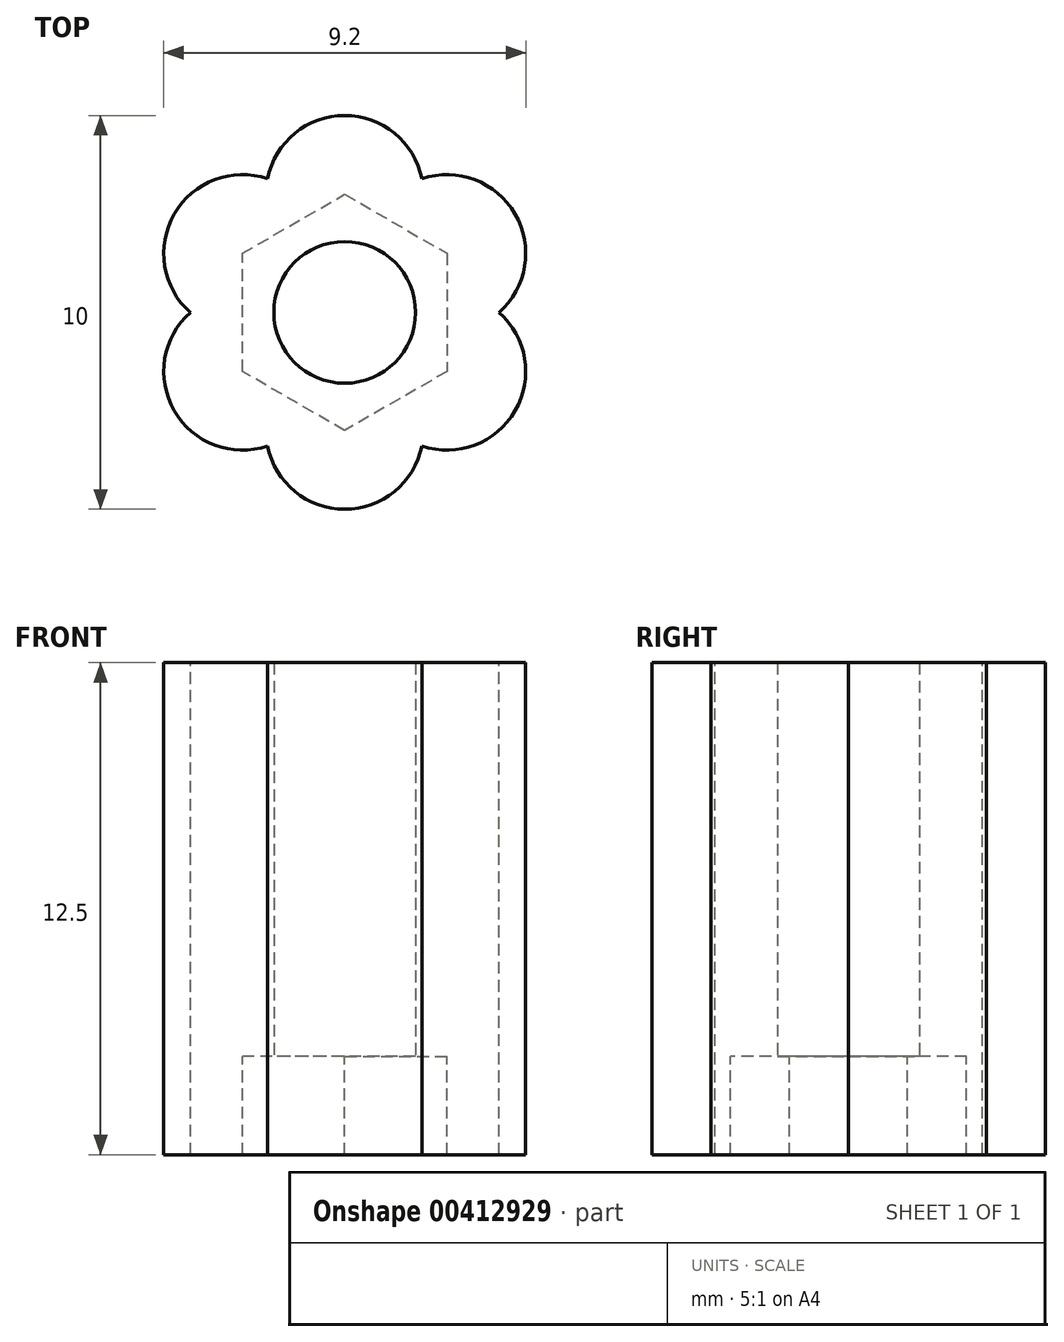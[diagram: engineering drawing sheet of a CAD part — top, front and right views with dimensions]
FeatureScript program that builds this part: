
annotation { "Feature Type Name" : "Feature", "Feature Type Description" : "" }
export const myFeature = defineFeature(function(context is Context, id is Id, definition is map)
    precondition{}
    {
        {
            var Q0;
            Q0=qCreatedBy(makeId("Top.planeOp"),FACE);
            var sketch = newSketch(context, id + "F0", { "sketchPlane" : qUnion([Q0])});
            skCircle(sketch, "E0.cCircle", {"center": v(0, 0) * mm, "radius": 3 * mm, "construction": true});
            skLineSegment(sketch, "E0.0", {"start": v(0, 3) * mm, "end": v(2.6, 1.5) * mm});
            skLineSegment(sketch, "E0.1", {"start": v(2.6, 1.5) * mm, "end": v(2.6, -1.5) * mm});
            skLineSegment(sketch, "E0.2", {"start": v(2.6, -1.5) * mm, "end": v(0, -3) * mm});
            skLineSegment(sketch, "E0.3", {"start": v(0, -3) * mm, "end": v(-2.6, -1.5) * mm});
            skLineSegment(sketch, "E0.4", {"start": v(-2.6, -1.5) * mm, "end": v(-2.6, 1.5) * mm});
            skLineSegment(sketch, "E0.5", {"start": v(-2.6, 1.5) * mm, "end": v(0, 3) * mm});
            skCircle(sketch, "E1", {"center": v(0, 0) * mm, "radius": 1.8 * mm});
            skCircle(sketch, "E2", {"center": v(0, 3) * mm, "radius": 2 * mm});
            skCircle(sketch, "E3", {"center": v(2.6, 1.5) * mm, "radius": 2 * mm});
            skCircle(sketch, "E4", {"center": v(2.6, -1.5) * mm, "radius": 2 * mm});
            skCircle(sketch, "E5", {"center": v(0, -3) * mm, "radius": 2 * mm});
            skCircle(sketch, "E6", {"center": v(-2.6, -1.5) * mm, "radius": 2 * mm});
            skCircle(sketch, "E7", {"center": v(-2.6, 1.5) * mm, "radius": 2 * mm});
            skSolve(sketch);
        }
        {
            var Q0;
            {var subQ3=sQuery(id+"F0.wireOp",EDGE,"E0.0");var subQ7=sQuery(id+"F0.wireOp",EDGE,"E0.5");var subQ9=makeQuery(id+"F0.imprint","INTERSECT",VERTEX,{"derivedFrom":[subQ3,subQ7]});Q0=makeQuery(id+"F0.imprint","IMPRINT",FACE,{"disambiguationData":[TD([[makeQuery(id+"F0.imprint","IMPRINT",EDGE,{"disambiguationData":[TD([[subQ9,-1.0]])],"derivedFrom":subQ3}),1.0]])]});}
            var Q1;
            {var subQ0=sQuery(id+"F0.wireOp",EDGE,"E3");var subQ1=sQuery(id+"F0.wireOp",EDGE,"E0.0");var subQ2=makeQuery(id+"F0.imprint","INTERSECT",VERTEX,{"derivedFrom":[subQ1,subQ0]});Q1=makeQuery(id+"F0.imprint","IMPRINT",FACE,{"disambiguationData":[TD([[makeQuery(id+"F0.imprint","IMPRINT",EDGE,{"disambiguationData":[TD([[subQ2,-1.0]])],"derivedFrom":subQ1}),1.0]])]});}
            var Q2;
            {var subQ0=sQuery(id+"F0.wireOp",EDGE,"E2");var subQ1=sQuery(id+"F0.wireOp",EDGE,"E0.5");var subQ2=makeQuery(id+"F0.imprint","INTERSECT",VERTEX,{"derivedFrom":[subQ1,subQ0]});Q2=makeQuery(id+"F0.imprint","IMPRINT",FACE,{"disambiguationData":[TD([[makeQuery(id+"F0.imprint","IMPRINT",EDGE,{"disambiguationData":[TD([[subQ2,-1.0]])],"derivedFrom":subQ1}),1.0]])]});}
            var Q3;
            {var subQ3=sQuery(id+"F0.wireOp",EDGE,"E0.5");var subQ7=sQuery(id+"F0.wireOp",EDGE,"E0.4");var subQ9=makeQuery(id+"F0.imprint","INTERSECT",VERTEX,{"derivedFrom":[subQ7,subQ3]});Q3=makeQuery(id+"F0.imprint","IMPRINT",FACE,{"disambiguationData":[TD([[makeQuery(id+"F0.imprint","IMPRINT",EDGE,{"disambiguationData":[TD([[subQ9,1.0]])],"derivedFrom":subQ7}),1.0]])]});}
            var Q4;
            {var subQ0=sQuery(id+"F0.wireOp",EDGE,"E7");var subQ1=sQuery(id+"F0.wireOp",EDGE,"E0.4");var subQ2=makeQuery(id+"F0.imprint","INTERSECT",VERTEX,{"derivedFrom":[subQ1,subQ0]});Q4=makeQuery(id+"F0.imprint","IMPRINT",FACE,{"disambiguationData":[TD([[makeQuery(id+"F0.imprint","IMPRINT",EDGE,{"disambiguationData":[TD([[subQ2,-1.0]])],"derivedFrom":subQ1}),1.0]])]});}
            var Q5;
            {var subQ3=sQuery(id+"F0.wireOp",EDGE,"E0.3");var subQ5=sQuery(id+"F0.wireOp",EDGE,"E0.4");var subQ6=makeQuery(id+"F0.imprint","INTERSECT",VERTEX,{"derivedFrom":[subQ3,subQ5]});Q5=makeQuery(id+"F0.imprint","IMPRINT",FACE,{"disambiguationData":[TD([[makeQuery(id+"F0.imprint","IMPRINT",EDGE,{"disambiguationData":[TD([[subQ6,1.0]])],"derivedFrom":subQ3}),1.0]])]});}
            var Q6;
            {var subQ0=sQuery(id+"F0.wireOp",EDGE,"E6");var subQ1=sQuery(id+"F0.wireOp",EDGE,"E0.3");var subQ2=makeQuery(id+"F0.imprint","INTERSECT",VERTEX,{"derivedFrom":[subQ1,subQ0]});Q6=makeQuery(id+"F0.imprint","IMPRINT",FACE,{"disambiguationData":[TD([[makeQuery(id+"F0.imprint","IMPRINT",EDGE,{"disambiguationData":[TD([[subQ2,-1.0]])],"derivedFrom":subQ1}),1.0]])]});}
            var Q7;
            {var subQ5=sQuery(id+"F0.wireOp",EDGE,"E0.2");var subQ7=sQuery(id+"F0.wireOp",EDGE,"E0.3");var subQ8=makeQuery(id+"F0.imprint","INTERSECT",VERTEX,{"derivedFrom":[subQ5,subQ7]});Q7=makeQuery(id+"F0.imprint","IMPRINT",FACE,{"disambiguationData":[TD([[makeQuery(id+"F0.imprint","IMPRINT",EDGE,{"disambiguationData":[TD([[subQ8,1.0]])],"derivedFrom":subQ5}),1.0]])]});}
            var Q8;
            {var subQ0=sQuery(id+"F0.wireOp",EDGE,"E5");var subQ1=sQuery(id+"F0.wireOp",EDGE,"E0.2");var subQ2=makeQuery(id+"F0.imprint","INTERSECT",VERTEX,{"derivedFrom":[subQ1,subQ0]});Q8=makeQuery(id+"F0.imprint","IMPRINT",FACE,{"disambiguationData":[TD([[makeQuery(id+"F0.imprint","IMPRINT",EDGE,{"disambiguationData":[TD([[subQ2,-1.0]])],"derivedFrom":subQ1}),1.0]])]});}
            var Q9;
            {var subQ5=sQuery(id+"F0.wireOp",EDGE,"E0.1");var subQ7=sQuery(id+"F0.wireOp",EDGE,"E0.2");var subQ8=makeQuery(id+"F0.imprint","INTERSECT",VERTEX,{"derivedFrom":[subQ5,subQ7]});Q9=makeQuery(id+"F0.imprint","IMPRINT",FACE,{"disambiguationData":[TD([[makeQuery(id+"F0.imprint","IMPRINT",EDGE,{"disambiguationData":[TD([[subQ8,1.0]])],"derivedFrom":subQ5}),1.0]])]});}
            var Q10;
            {var subQ0=sQuery(id+"F0.wireOp",EDGE,"E4");var subQ1=sQuery(id+"F0.wireOp",EDGE,"E0.1");var subQ2=makeQuery(id+"F0.imprint","INTERSECT",VERTEX,{"derivedFrom":[subQ1,subQ0]});Q10=makeQuery(id+"F0.imprint","IMPRINT",FACE,{"disambiguationData":[TD([[makeQuery(id+"F0.imprint","IMPRINT",EDGE,{"disambiguationData":[TD([[subQ2,-1.0]])],"derivedFrom":subQ1}),1.0]])]});}
            var Q11;
            {var subQ5=sQuery(id+"F0.wireOp",EDGE,"E0.1");var subQ6=sQuery(id+"F0.wireOp",EDGE,"E0.0");var subQ7=makeQuery(id+"F0.imprint","INTERSECT",VERTEX,{"derivedFrom":[subQ6,subQ5]});Q11=makeQuery(id+"F0.imprint","IMPRINT",FACE,{"disambiguationData":[TD([[makeQuery(id+"F0.imprint","IMPRINT",EDGE,{"disambiguationData":[TD([[subQ7,1.0]])],"derivedFrom":subQ6}),1.0]])]});}
            extrude(context, id + "F1", {"entities" : qUnion([Q0, Q1, Q2, Q3, Q4, Q5, Q6, Q7, Q8, Q9, Q10, Q11]), "oppositeDirection" : true, "depth" : 2.5 * mm, "offsetDistance" : 25 * mm});
        }
        {
            var Q0;
            {var subQ5=sQuery(id+"F0.wireOp",EDGE,"E0.2");var subQ7=sQuery(id+"F0.wireOp",EDGE,"E0.3");var subQ8=makeQuery(id+"F0.imprint","INTERSECT",VERTEX,{"derivedFrom":[subQ5,subQ7]});Q0=makeQuery(id+"F0.imprint","IMPRINT",FACE,{"disambiguationData":[TD([[makeQuery(id+"F0.imprint","IMPRINT",EDGE,{"disambiguationData":[TD([[subQ8,1.0]])],"derivedFrom":subQ5}),1.0]])]});}
            var Q1;
            {var subQ0=sQuery(id+"F0.wireOp",EDGE,"E6");var subQ1=sQuery(id+"F0.wireOp",EDGE,"E0.3");var subQ2=makeQuery(id+"F0.imprint","INTERSECT",VERTEX,{"derivedFrom":[subQ1,subQ0]});Q1=makeQuery(id+"F0.imprint","IMPRINT",FACE,{"disambiguationData":[TD([[makeQuery(id+"F0.imprint","IMPRINT",EDGE,{"disambiguationData":[TD([[subQ2,-1.0]])],"derivedFrom":subQ1}),1.0]])]});}
            var Q2;
            {var subQ0=sQuery(id+"F0.wireOp",EDGE,"E5");var subQ1=sQuery(id+"F0.wireOp",EDGE,"E0.2");var subQ2=makeQuery(id+"F0.imprint","INTERSECT",VERTEX,{"derivedFrom":[subQ1,subQ0]});Q2=makeQuery(id+"F0.imprint","IMPRINT",FACE,{"disambiguationData":[TD([[makeQuery(id+"F0.imprint","IMPRINT",EDGE,{"disambiguationData":[TD([[subQ2,-1.0]])],"derivedFrom":subQ1}),1.0]])]});}
            var Q3;
            {var subQ5=sQuery(id+"F0.wireOp",EDGE,"E0.1");var subQ7=sQuery(id+"F0.wireOp",EDGE,"E0.2");var subQ8=makeQuery(id+"F0.imprint","INTERSECT",VERTEX,{"derivedFrom":[subQ5,subQ7]});Q3=makeQuery(id+"F0.imprint","IMPRINT",FACE,{"disambiguationData":[TD([[makeQuery(id+"F0.imprint","IMPRINT",EDGE,{"disambiguationData":[TD([[subQ8,1.0]])],"derivedFrom":subQ5}),1.0]])]});}
            var Q4;
            {var subQ0=sQuery(id+"F0.wireOp",EDGE,"E5");var subQ1=sQuery(id+"F0.wireOp",EDGE,"E0.2");var subQ2=makeQuery(id+"F0.imprint","INTERSECT",VERTEX,{"derivedFrom":[subQ1,subQ0]});Q4=makeQuery(id+"F0.imprint","IMPRINT",FACE,{"disambiguationData":[TD([[makeQuery(id+"F0.imprint","IMPRINT",EDGE,{"disambiguationData":[TD([[subQ2,-1.0]])],"derivedFrom":subQ1}),-1.0]])]});}
            var Q5;
            {var subQ1=sQuery(id+"F0.wireOp",EDGE,"E0.2");var subQ7=sQuery(id+"F0.wireOp",EDGE,"E0.3");var subQ8=makeQuery(id+"F0.imprint","INTERSECT",VERTEX,{"derivedFrom":[subQ1,subQ7]});Q5=makeQuery(id+"F0.imprint","IMPRINT",FACE,{"disambiguationData":[TD([[makeQuery(id+"F0.imprint","IMPRINT",EDGE,{"disambiguationData":[TD([[subQ8,1.0]])],"derivedFrom":subQ1}),-1.0]])]});}
            var Q6;
            {var subQ1=sQuery(id+"F0.wireOp",EDGE,"E0.1");var subQ6=sQuery(id+"F0.wireOp",EDGE,"E0.2");var subQ9=makeQuery(id+"F0.imprint","INTERSECT",VERTEX,{"derivedFrom":[subQ1,subQ6]});Q6=makeQuery(id+"F0.imprint","IMPRINT",FACE,{"disambiguationData":[TD([[makeQuery(id+"F0.imprint","IMPRINT",EDGE,{"disambiguationData":[TD([[subQ9,1.0]])],"derivedFrom":subQ1}),-1.0]])]});}
            var Q7;
            {var subQ0=sQuery(id+"F0.wireOp",EDGE,"E6");var subQ1=sQuery(id+"F0.wireOp",EDGE,"E0.3");var subQ2=makeQuery(id+"F0.imprint","INTERSECT",VERTEX,{"derivedFrom":[subQ1,subQ0]});Q7=makeQuery(id+"F0.imprint","IMPRINT",FACE,{"disambiguationData":[TD([[makeQuery(id+"F0.imprint","IMPRINT",EDGE,{"disambiguationData":[TD([[subQ2,-1.0]])],"derivedFrom":subQ1}),-1.0]])]});}
            var Q8;
            {var subQ3=sQuery(id+"F0.wireOp",EDGE,"E0.3");var subQ5=sQuery(id+"F0.wireOp",EDGE,"E0.4");var subQ6=makeQuery(id+"F0.imprint","INTERSECT",VERTEX,{"derivedFrom":[subQ3,subQ5]});Q8=makeQuery(id+"F0.imprint","IMPRINT",FACE,{"disambiguationData":[TD([[makeQuery(id+"F0.imprint","IMPRINT",EDGE,{"disambiguationData":[TD([[subQ6,1.0]])],"derivedFrom":subQ3}),1.0]])]});}
            var Q9;
            {var subQ1=sQuery(id+"F0.wireOp",EDGE,"E0.3");var subQ7=sQuery(id+"F0.wireOp",EDGE,"E0.4");var subQ8=makeQuery(id+"F0.imprint","INTERSECT",VERTEX,{"derivedFrom":[subQ1,subQ7]});Q9=makeQuery(id+"F0.imprint","IMPRINT",FACE,{"disambiguationData":[TD([[makeQuery(id+"F0.imprint","IMPRINT",EDGE,{"disambiguationData":[TD([[subQ8,1.0]])],"derivedFrom":subQ1}),-1.0]])]});}
            var Q10;
            {var subQ0=sQuery(id+"F0.wireOp",EDGE,"E4");var subQ1=sQuery(id+"F0.wireOp",EDGE,"E0.1");var subQ2=makeQuery(id+"F0.imprint","INTERSECT",VERTEX,{"derivedFrom":[subQ1,subQ0]});Q10=makeQuery(id+"F0.imprint","IMPRINT",FACE,{"disambiguationData":[TD([[makeQuery(id+"F0.imprint","IMPRINT",EDGE,{"disambiguationData":[TD([[subQ2,-1.0]])],"derivedFrom":subQ1}),1.0]])]});}
            var Q11;
            {var subQ5=sQuery(id+"F0.wireOp",EDGE,"E0.1");var subQ6=sQuery(id+"F0.wireOp",EDGE,"E0.0");var subQ7=makeQuery(id+"F0.imprint","INTERSECT",VERTEX,{"derivedFrom":[subQ6,subQ5]});Q11=makeQuery(id+"F0.imprint","IMPRINT",FACE,{"disambiguationData":[TD([[makeQuery(id+"F0.imprint","IMPRINT",EDGE,{"disambiguationData":[TD([[subQ7,1.0]])],"derivedFrom":subQ6}),1.0]])]});}
            var Q12;
            {var subQ0=sQuery(id+"F0.wireOp",EDGE,"E3");var subQ1=sQuery(id+"F0.wireOp",EDGE,"E0.0");var subQ2=makeQuery(id+"F0.imprint","INTERSECT",VERTEX,{"derivedFrom":[subQ1,subQ0]});Q12=makeQuery(id+"F0.imprint","IMPRINT",FACE,{"disambiguationData":[TD([[makeQuery(id+"F0.imprint","IMPRINT",EDGE,{"disambiguationData":[TD([[subQ2,-1.0]])],"derivedFrom":subQ1}),1.0]])]});}
            var Q13;
            {var subQ0=sQuery(id+"F0.wireOp",EDGE,"E4");var subQ1=sQuery(id+"F0.wireOp",EDGE,"E0.1");var subQ2=makeQuery(id+"F0.imprint","INTERSECT",VERTEX,{"derivedFrom":[subQ1,subQ0]});Q13=makeQuery(id+"F0.imprint","IMPRINT",FACE,{"disambiguationData":[TD([[makeQuery(id+"F0.imprint","IMPRINT",EDGE,{"disambiguationData":[TD([[subQ2,-1.0]])],"derivedFrom":subQ1}),-1.0]])]});}
            var Q14;
            {var subQ1=sQuery(id+"F0.wireOp",EDGE,"E0.0");var subQ5=sQuery(id+"F0.wireOp",EDGE,"E0.1");var subQ6=makeQuery(id+"F0.imprint","INTERSECT",VERTEX,{"derivedFrom":[subQ1,subQ5]});Q14=makeQuery(id+"F0.imprint","IMPRINT",FACE,{"disambiguationData":[TD([[makeQuery(id+"F0.imprint","IMPRINT",EDGE,{"disambiguationData":[TD([[subQ6,1.0]])],"derivedFrom":subQ1}),-1.0]])]});}
            var Q15;
            {var subQ0=sQuery(id+"F0.wireOp",EDGE,"E3");var subQ1=sQuery(id+"F0.wireOp",EDGE,"E0.0");var subQ2=makeQuery(id+"F0.imprint","INTERSECT",VERTEX,{"derivedFrom":[subQ1,subQ0]});Q15=makeQuery(id+"F0.imprint","IMPRINT",FACE,{"disambiguationData":[TD([[makeQuery(id+"F0.imprint","IMPRINT",EDGE,{"disambiguationData":[TD([[subQ2,-1.0]])],"derivedFrom":subQ1}),-1.0]])]});}
            var Q16;
            {var subQ0=sQuery(id+"F0.wireOp",EDGE,"E7");var subQ1=sQuery(id+"F0.wireOp",EDGE,"E0.4");var subQ2=makeQuery(id+"F0.imprint","INTERSECT",VERTEX,{"derivedFrom":[subQ1,subQ0]});Q16=makeQuery(id+"F0.imprint","IMPRINT",FACE,{"disambiguationData":[TD([[makeQuery(id+"F0.imprint","IMPRINT",EDGE,{"disambiguationData":[TD([[subQ2,-1.0]])],"derivedFrom":subQ1}),1.0]])]});}
            var Q17;
            {var subQ3=sQuery(id+"F0.wireOp",EDGE,"E0.5");var subQ7=sQuery(id+"F0.wireOp",EDGE,"E0.4");var subQ9=makeQuery(id+"F0.imprint","INTERSECT",VERTEX,{"derivedFrom":[subQ7,subQ3]});Q17=makeQuery(id+"F0.imprint","IMPRINT",FACE,{"disambiguationData":[TD([[makeQuery(id+"F0.imprint","IMPRINT",EDGE,{"disambiguationData":[TD([[subQ9,1.0]])],"derivedFrom":subQ7}),1.0]])]});}
            var Q18;
            {var subQ0=sQuery(id+"F0.wireOp",EDGE,"E7");var subQ1=sQuery(id+"F0.wireOp",EDGE,"E0.4");var subQ2=makeQuery(id+"F0.imprint","INTERSECT",VERTEX,{"derivedFrom":[subQ1,subQ0]});Q18=makeQuery(id+"F0.imprint","IMPRINT",FACE,{"disambiguationData":[TD([[makeQuery(id+"F0.imprint","IMPRINT",EDGE,{"disambiguationData":[TD([[subQ2,-1.0]])],"derivedFrom":subQ1}),-1.0]])]});}
            var Q19;
            {var subQ1=sQuery(id+"F0.wireOp",EDGE,"E0.5");var subQ7=sQuery(id+"F0.wireOp",EDGE,"E0.4");var subQ8=makeQuery(id+"F0.imprint","INTERSECT",VERTEX,{"derivedFrom":[subQ7,subQ1]});Q19=makeQuery(id+"F0.imprint","IMPRINT",FACE,{"disambiguationData":[TD([[makeQuery(id+"F0.imprint","IMPRINT",EDGE,{"disambiguationData":[TD([[subQ8,1.0]])],"derivedFrom":subQ7}),-1.0]])]});}
            var Q20;
            {var subQ0=sQuery(id+"F0.wireOp",EDGE,"E2");var subQ1=sQuery(id+"F0.wireOp",EDGE,"E0.5");var subQ2=makeQuery(id+"F0.imprint","INTERSECT",VERTEX,{"derivedFrom":[subQ1,subQ0]});Q20=makeQuery(id+"F0.imprint","IMPRINT",FACE,{"disambiguationData":[TD([[makeQuery(id+"F0.imprint","IMPRINT",EDGE,{"disambiguationData":[TD([[subQ2,-1.0]])],"derivedFrom":subQ1}),1.0]])]});}
            var Q21;
            {var subQ3=sQuery(id+"F0.wireOp",EDGE,"E0.0");var subQ7=sQuery(id+"F0.wireOp",EDGE,"E0.5");var subQ9=makeQuery(id+"F0.imprint","INTERSECT",VERTEX,{"derivedFrom":[subQ3,subQ7]});Q21=makeQuery(id+"F0.imprint","IMPRINT",FACE,{"disambiguationData":[TD([[makeQuery(id+"F0.imprint","IMPRINT",EDGE,{"disambiguationData":[TD([[subQ9,-1.0]])],"derivedFrom":subQ3}),1.0]])]});}
            var Q22;
            {var subQ0=sQuery(id+"F0.wireOp",EDGE,"E2");var subQ1=sQuery(id+"F0.wireOp",EDGE,"E0.5");var subQ2=makeQuery(id+"F0.imprint","INTERSECT",VERTEX,{"derivedFrom":[subQ1,subQ0]});Q22=makeQuery(id+"F0.imprint","IMPRINT",FACE,{"disambiguationData":[TD([[makeQuery(id+"F0.imprint","IMPRINT",EDGE,{"disambiguationData":[TD([[subQ2,-1.0]])],"derivedFrom":subQ1}),-1.0]])]});}
            var Q23;
            {var subQ1=sQuery(id+"F0.wireOp",EDGE,"E0.0");var subQ5=sQuery(id+"F0.wireOp",EDGE,"E0.5");var subQ6=makeQuery(id+"F0.imprint","INTERSECT",VERTEX,{"derivedFrom":[subQ1,subQ5]});Q23=makeQuery(id+"F0.imprint","IMPRINT",FACE,{"disambiguationData":[TD([[makeQuery(id+"F0.imprint","IMPRINT",EDGE,{"disambiguationData":[TD([[subQ6,-1.0]])],"derivedFrom":subQ1}),-1.0]])]});}
            extrude(context, id + "F2", {"entities" : qUnion([Q0, Q1, Q2, Q3, Q4, Q5, Q6, Q7, Q8, Q9, Q10, Q11, Q12, Q13, Q14, Q15, Q16, Q17, Q18, Q19, Q20, Q21, Q22, Q23]), "operationType" : NewBodyOperationType.ADD, "depth" : 10 * mm, "offsetDistance" : 25 * mm});
        }
    });
